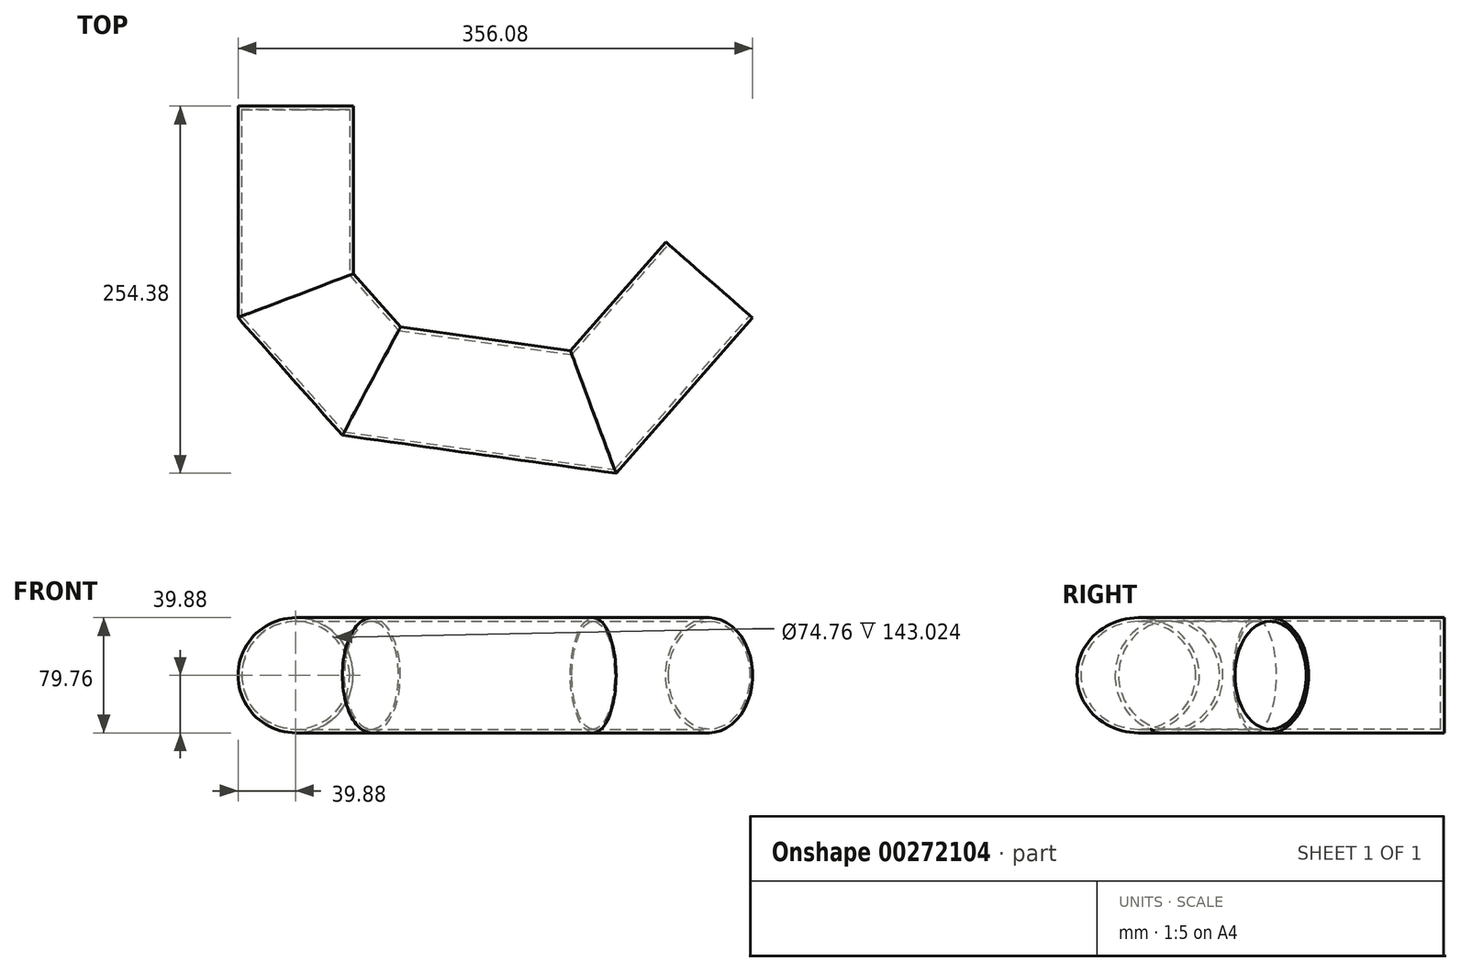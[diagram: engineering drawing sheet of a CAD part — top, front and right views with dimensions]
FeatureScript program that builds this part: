
annotation { "Feature Type Name" : "Feature", "Feature Type Description" : "" }
export const myFeature = defineFeature(function(context is Context, id is Id, definition is map)
    precondition{}
    {
        {
            var Q0;
            Q0=qCreatedBy(makeId("Front.planeOp"),FACE);
            var sketch = newSketch(context, id + "F0", { "sketchPlane" : qUnion([Q0])});
            skCircle(sketch, "E0", {"center": v(0, 0) * mm, "radius": 39.88 * mm});
            skSolve(sketch);
        }
        {
            var Q0;
            Q0=qCreatedBy(makeId("Front.planeOp"),FACE);
            cPlane(context, id + "F1", {"entities" : qUnion([Q0]), "cplaneType" : CPlaneType.OFFSET, "offset" : 102.8 * mm, "width" : 150 * mm, "height" : 150 * mm});
        }
        {
            var Q0;
            Q0=qCreatedBy(makeId("Top.planeOp"),FACE);
            var sketch = newSketch(context, id + "F2", { "sketchPlane" : qUnion([Q0])});
            skLineSegment(sketch, "E1", {"start": v(0, 0) * mm, "end": v(0, -131.3) * mm});
            skLineSegment(sketch, "E2", {"start": v(0, -131.3) * mm, "end": v(52.46, -190.56) * mm});
            skLineSegment(sketch, "E3", {"start": v(52.46, -190.56) * mm, "end": v(205.95, -211.92) * mm});
            skLineSegment(sketch, "E4", {"start": v(205.95, -211.92) * mm, "end": v(286.21, -120.37) * mm});
            skSolve(sketch);
        }
        {
            var Q0;
            Q0=makeQuery(id+"F0.imprint","IMPRINT",FACE,{"disambiguationData":[TD([[makeQuery(id+"F0.imprint","IMPRINT",EDGE,{"derivedFrom":sQuery(id+"F0.wireOp",EDGE,"E0")}),1.0]])]});
            var Q1;
            Q1 = qConstructionFilter(qBodyType(qCreatedBy(id + "F2" ,EDGE), BodyType.WIRE), ConstructionObject.NO);
            sweep(context, id + "F3", {"profiles" : qUnion([Q0]), "path" : qUnion([Q1])});
        }
        {
            var Q0;
            Q0=makeQuery(id+"F3.opSweep","CAP_FACE",FACE,{"disambiguationData":[OSD([sQuery(id+"F0.wireOp",EDGE,"E0"),sQuery(id+"F2.wireOp",VERTEX,"E4.end")])],"isStart":false});
            shell(context, id + "F4", {"entities" : qUnion([Q0]), "thickness" : 2.5 * mm});
        }
    });
